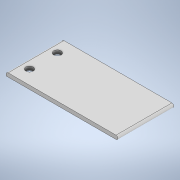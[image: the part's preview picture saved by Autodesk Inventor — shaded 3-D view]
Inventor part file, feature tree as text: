
AUTODESK INVENTOR PART (.ipt)
format: ipt  version: 2020 (Build 240168000, 168)  size: 111,104 bytes
history: native  units: in
note: dims shown in document units (in); Inventor stores cm internally (conversion verified against a paired STEP export)
features: fillet x2, sketch x2, extrude x1, hole x1
ambient origin geometry x8: Origin, YZ Plane, XZ Plane, XY Plane, X Axis, Y Axis, Z Axis, Center Point
bodies: Solid1 (feature_tree)
feature tree (6):
  extrude  "Extrusion1"  Depth=1.5in
  hole  "Hole1"  [1 undecoded]
  fillet  "Fillet1"  Radius=0.375in
  fillet  "Fillet2"  Radius=0.375in
  sketch  "Sketch1"  dims[d0=3.0in d1=1.5in]
  sketch  "Sketch2"  dims[d2=0.1in d3=0.0in d4=0.25in d5=0.375in d6=0.375in d7=0.2in d8=0.75in d9=0.375in d10=0.25in d11=0.5635in d12=0.5in d13=0.8108in d14=0.05in d15=0.05in]
note: 1 required parameter value undecoded (feature->parameter linkage not recoverable at this tier; creation-order binding heuristic only, values carry confidence <= 0.55)
